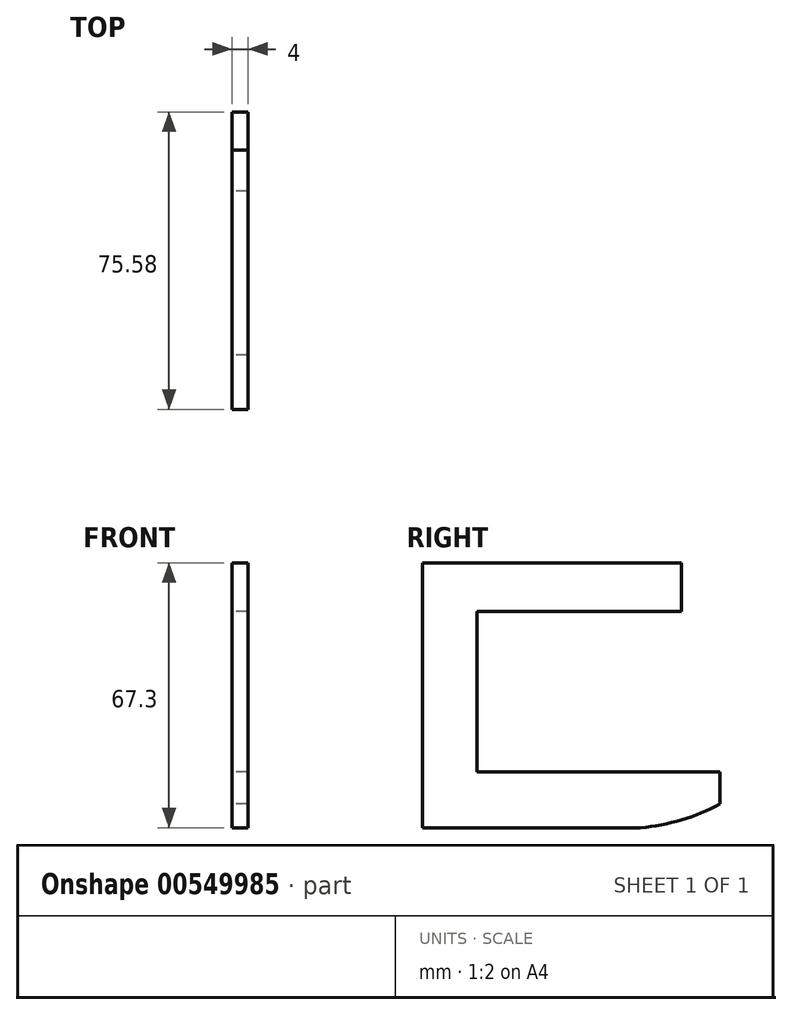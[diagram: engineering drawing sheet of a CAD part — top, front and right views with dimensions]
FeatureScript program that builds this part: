
annotation { "Feature Type Name" : "Feature", "Feature Type Description" : "" }
export const myFeature = defineFeature(function(context is Context, id is Id, definition is map)
    precondition{}
    {
        {
            var Q0;
            Q0=qCreatedBy(makeId("Right.planeOp"),FACE);
            var sketch = newSketch(context, id + "F0", { "sketchPlane" : qUnion([Q0])});
            skLineSegment(sketch, "E0", {"start": v(0, 0) * mm, "end": v(0, 67.3) * mm});
            skLineSegment(sketch, "E1", {"start": v(0, 67.3) * mm, "end": v(65.83, 67.3) * mm});
            skLineSegment(sketch, "E2", {"start": v(65.83, 67.3) * mm, "end": v(65.83, 54.94) * mm});
            skLineSegment(sketch, "E3", {"start": v(55.4, 0) * mm, "end": v(0, 0) * mm});
            skArc(sketch, "E4", {"start": v(55.4, 0) * mm, "mid": v(65.8, 1.98) * mm, "end": v(75.58, 6) * mm});
            skLineSegment(sketch, "E5", {"start": v(65.83, 54.94) * mm, "end": v(13.83, 54.94) * mm});
            skLineSegment(sketch, "E6", {"start": v(13.83, 54.94) * mm, "end": v(13.83, 14.14) * mm});
            skLineSegment(sketch, "E7", {"start": v(13.83, 14.14) * mm, "end": v(75.58, 14.14) * mm});
            skLineSegment(sketch, "E8", {"start": v(75.58, 14.14) * mm, "end": v(75.58, 6) * mm});
            skSolve(sketch);
        }
        {
            var Q0;
            Q0 = qSketchRegion(id + "F0", true);
            extrude(context, id + "F1", {"entities" : qUnion([Q0]), "depth" : 4 * mm, "offsetDistance" : 25 * mm});
        }
    });
